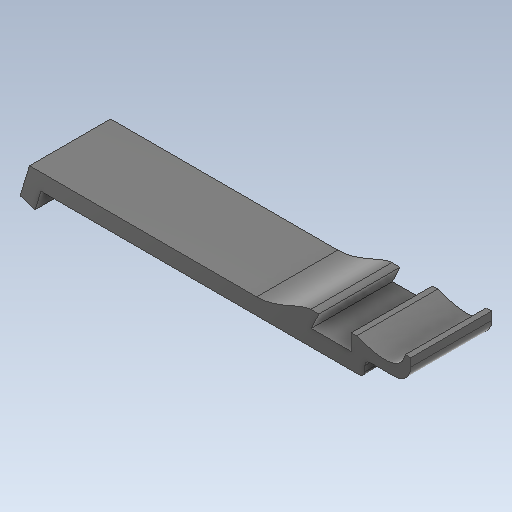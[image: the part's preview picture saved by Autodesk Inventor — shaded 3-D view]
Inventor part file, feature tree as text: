
AUTODESK INVENTOR PART (.ipt)
format: ipt  version: 2020 (Build 240168000, 168)  size: 220,672 bytes
history: native  units: mm
features: extrude x4, sketch x3, projected_geometry x2, other x1
ambient origin geometry x8: Origin, YZ Plane, XZ Plane, XY Plane, X Axis, Y Axis, Z Axis, Center Point
bodies: Body1 (feature_tree)
feature tree (10):
  other  "Твердое тело1"
  extrude  "Выдавливание1"  Depth=9.0mm
  extrude  "Выдавливание2"  Depth=3.0mm
  sketch  "Эскиз4"
  extrude  "Выдавливание3"  Depth=3.0mm
  extrude  "Выдавливание4"  Depth=2.5mm
  sketch  "Эскиз1"
  sketch  "Эскиз3"
  projected_geometry  "Спроецированная петля1"
  projected_geometry  "Спроецированная петля2"
